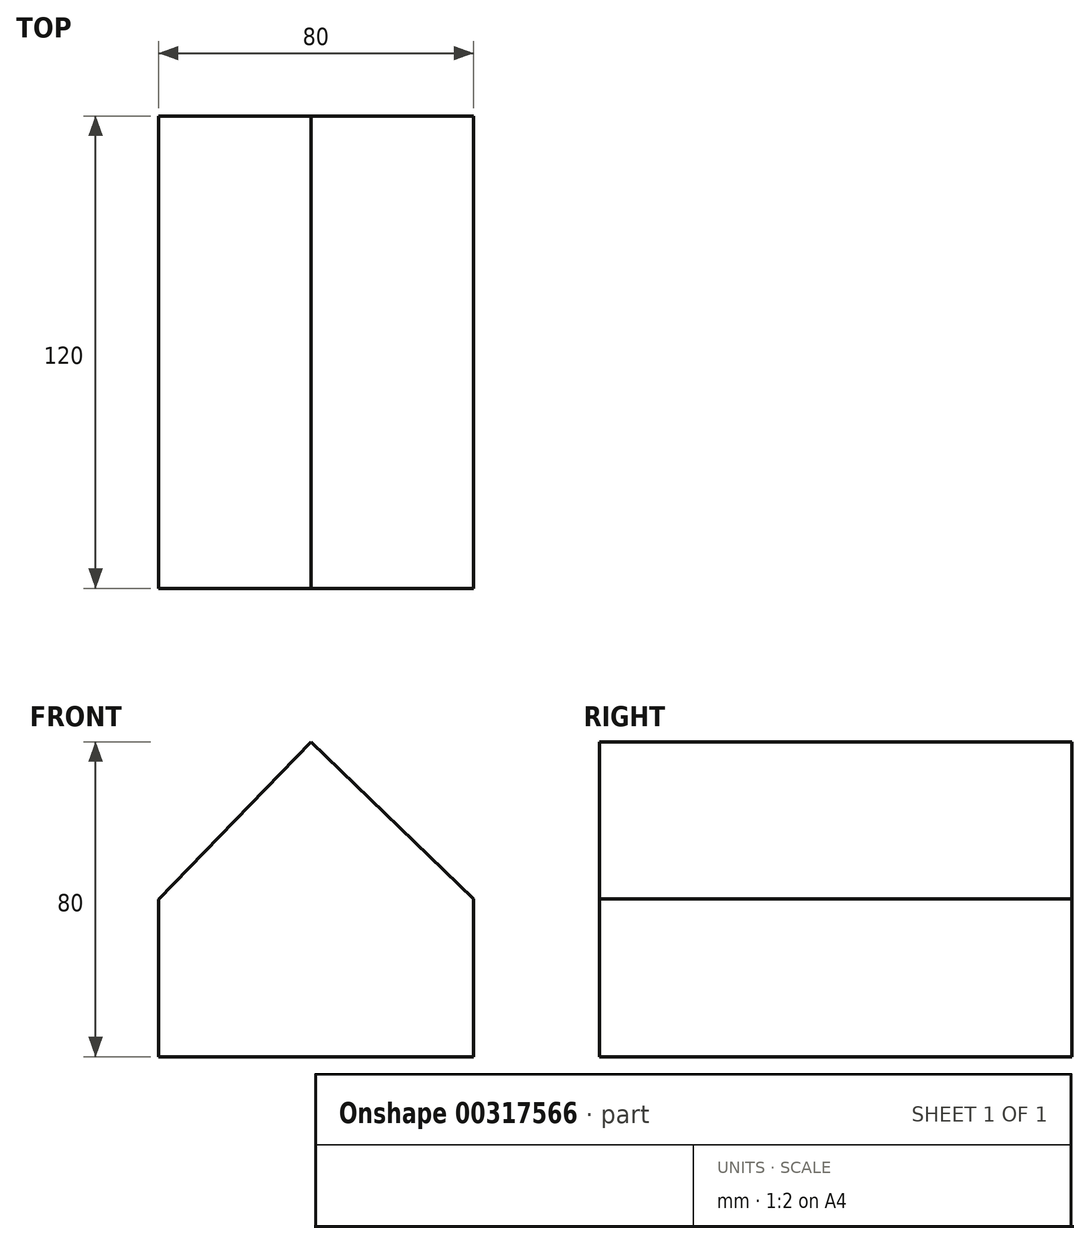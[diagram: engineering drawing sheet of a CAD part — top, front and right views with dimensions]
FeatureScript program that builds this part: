
annotation { "Feature Type Name" : "Feature", "Feature Type Description" : "" }
export const myFeature = defineFeature(function(context is Context, id is Id, definition is map)
    precondition{}
    {
        {
            var Q0;
            Q0=qCreatedBy(makeId("Front.planeOp"),FACE);
            var sketch = newSketch(context, id + "F0", { "sketchPlane" : qUnion([Q0])});
            skLineSegment(sketch, "E0.bottom", {"start": v(-38.8, 53.88) * mm, "end": v(41.2, 53.88) * mm});
            skLineSegment(sketch, "E0.top", {"start": v(-38.8, -26.12) * mm, "end": v(41.2, -26.12) * mm});
            skLineSegment(sketch, "E0.left", {"start": v(-38.8, 53.88) * mm, "end": v(-38.8, -26.12) * mm});
            skLineSegment(sketch, "E0.right", {"start": v(41.2, 53.88) * mm, "end": v(41.2, -26.12) * mm});
            skSolve(sketch);
        }
        {
            var Q0;
            Q0=makeQuery(id+"F0.imprint","IMPRINT",FACE,{"disambiguationData":[TD([[makeQuery(id+"F0.imprint","IMPRINT",EDGE,{"derivedFrom":sQuery(id+"F0.wireOp",EDGE,"E0.bottom")}),-1.0]])]});
            extrude(context, id + "F1", {"entities" : qUnion([Q0]), "depth" : 120 * mm});
        }
        {
            var Q0;
            Q0=makeQuery(id+"F1.opExtrude","CAP_FACE",FACE,{"disambiguationData":[OSD([sQuery(id+"F0.wireOp",EDGE,"E0.bottom"),sQuery(id+"F0.wireOp",EDGE,"E0.top"),sQuery(id+"F0.wireOp",EDGE,"E0.left"),sQuery(id+"F0.wireOp",EDGE,"E0.right")])],"isStart":false});
            var sketch = newSketch(context, id + "F2", { "sketchPlane" : qUnion([Q0])});
            skLineSegment(sketch, "E1", {"start": v(-38.8, 13.88) * mm, "end": v(0, 53.88) * mm});
            skPoint(sketch, "E1.endSnap0", {"position": v(1.2, 53.88) * mm});
            skLineSegment(sketch, "E2", {"start": v(0, 53.88) * mm, "end": v(41.2, 13.91) * mm});
            skSolve(sketch);
        }
        {
            var Q0;
            {var subQ0=sQuery(id+"F2.wireOp",EDGE,"E1");Q0=makeQuery(id+"F2.imprint","IMPRINT",FACE,{"disambiguationData":[TD([[makeQuery(id+"F2.imprint","IMPRINT",EDGE,{"derivedFrom":subQ0}),1.0]])]});}
            var Q1;
            {var subQ0=sQuery(id+"F2.wireOp",EDGE,"E2");Q1=makeQuery(id+"F2.imprint","IMPRINT",FACE,{"disambiguationData":[TD([[makeQuery(id+"F2.imprint","IMPRINT",EDGE,{"derivedFrom":subQ0}),1.0]])]});}
            extrude(context, id + "F3", {"entities" : qUnion([Q0, Q1]), "operationType" : NewBodyOperationType.REMOVE, "endBound" : BoundingType.THROUGH_ALL, "oppositeDirection" : true, "depth" : 25 * mm});
        }
    });
